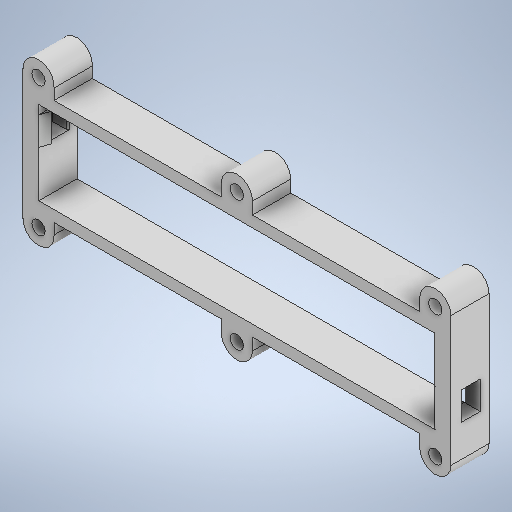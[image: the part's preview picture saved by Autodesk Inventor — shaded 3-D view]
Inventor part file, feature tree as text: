
AUTODESK INVENTOR PART (.ipt)
format: ipt  version: 2025.1 (Build 291241000, 241)  size: 364,032 bytes
history: native  units: mm
features: extrude x6, sketch x6, chamfer x4, plane x1
ambient origin geometry x8: Origin, YZ Plane, XZ Plane, XY Plane, X Axis, Y Axis, Z Axis, Center Point
bodies: Solid1 (feature_tree)
feature tree (17):
  extrude  "Extrusion1"  Depth=26.2mm
  sketch  "Sketch2"  dims[d2=3.5mm d3=3.5mm]
  sketch  "Sketch3"  dims[d4=124.5mm d5=12.0mm d6=0.0mm]
  extrude  "Extrusion2"  Depth=3.5mm
  extrude  "Extrusion3"  Depth=12.0mm TaperAngle=0.0deg
  extrude  "Extrusion4"  Depth=2.8mm
  extrude  "Extrusion5"  Depth=8.85mm
  chamfer  "Chamfer1"  Distance=2.8mm
  extrude  "Extrusion6"  Depth=5.8mm
  chamfer  "Chamfer2"  Distance=8.85mm
  chamfer  "Chamfer3"  Distance=12.0mm
  chamfer  "Chamfer4"  Distance=10.0mm
  plane  "Work Plane1"
  sketch  "Sketch1"  dims[d0=5.0mm d1=26.2mm]
  sketch  "Sketch4"  dims[d7=2.8mm d8=2.8mm]
  sketch  "Sketch5"  dims[d9=5.8mm d10=8.85mm]
  sketch  "Sketch6"  dims[d11=2.8mm d12=2.8mm d13=5.8mm d14=8.85mm d15=12.0mm d16=0.0mm d17=10.0mm d18=0.0mm d19=4.9mm d20=4.2mm d21=3.8mm d22=10.0mm d23=0.0mm d24=1.2mm d25=0.0mm d26=3.4mm d27=1.2mm d28=45.0deg d29=1.2mm d30=0.0mm d31=3.4mm d32=1.2mm d33=45.0deg d34=0.5mm d35=1.2mm d36=45.0deg d37=0.5mm d38=1.2mm d39=45.0deg d40=4.2mm]
